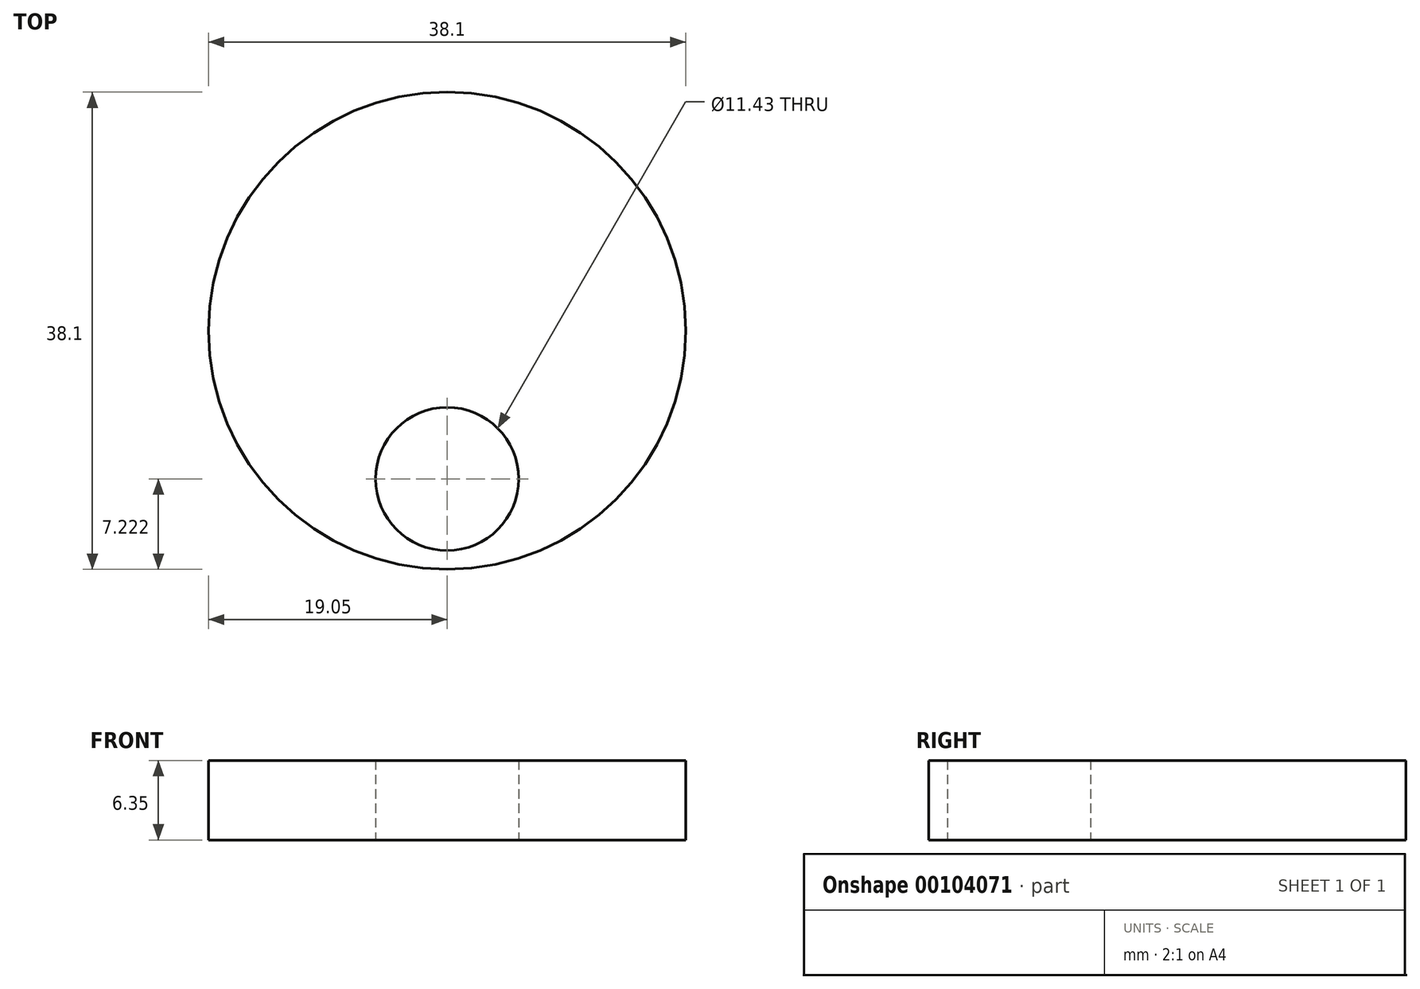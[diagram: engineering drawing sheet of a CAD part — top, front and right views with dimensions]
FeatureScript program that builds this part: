
annotation { "Feature Type Name" : "Feature", "Feature Type Description" : "" }
export const myFeature = defineFeature(function(context is Context, id is Id, definition is map)
    precondition{}
    {
        {
            var Q0;
            Q0=qCreatedBy(makeId("Top.planeOp"),FACE);
            var sketch = newSketch(context, id + "F0", { "sketchPlane" : qUnion([Q0])});
            skCircle(sketch, "E0", {"center": v(0, 0) * mm, "radius": 19.05 * mm});
            skCircle(sketch, "E1", {"center": v(0, -11.83) * mm, "radius": 5.72 * mm});
            skSolve(sketch);
        }
        {
            var Q0;
            Q0 = qSketchRegion(id + "F0", true);
            extrude(context, id + "F1", {"entities" : qUnion([Q0]), "depth" : 6.35 * mm});
        }
    });
